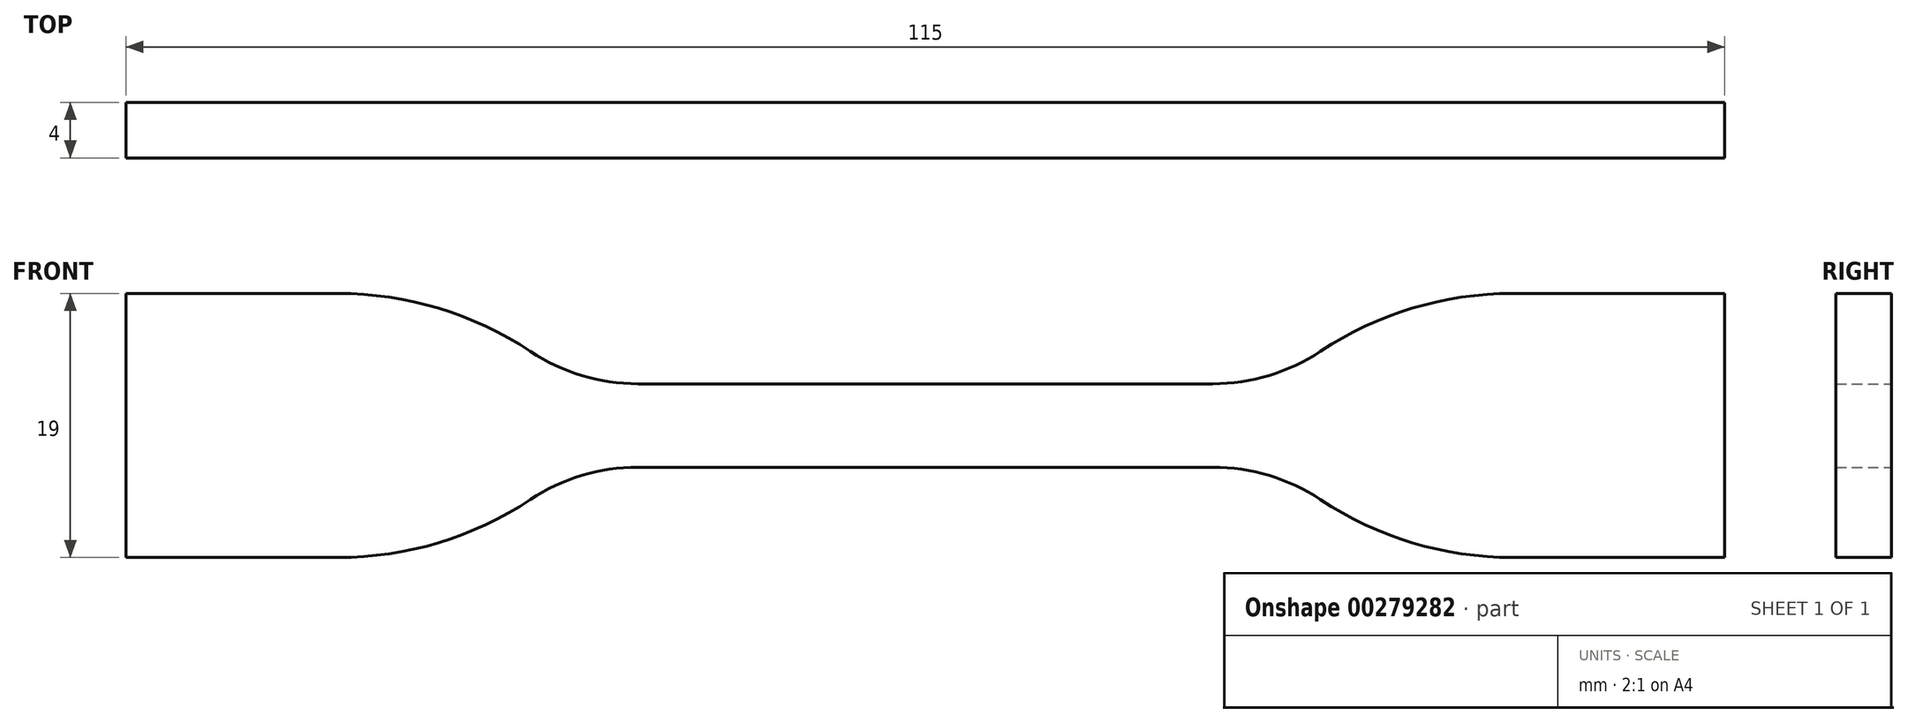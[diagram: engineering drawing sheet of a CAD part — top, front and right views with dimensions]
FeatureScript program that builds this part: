
annotation { "Feature Type Name" : "Feature", "Feature Type Description" : "" }
export const myFeature = defineFeature(function(context is Context, id is Id, definition is map)
    precondition{}
    {
        {
            var Q0;
            Q0=qCreatedBy(makeId("Front.planeOp"),FACE);
            var sketch = newSketch(context, id + "F0", { "sketchPlane" : qUnion([Q0])});
            skLineSegment(sketch, "E0", {"start": v(0, 3) * mm, "end": v(20.68, 3) * mm});
            skArc(sketch, "E1", {"start": v(20.68, 3) * mm, "mid": v(24.72, 3.6) * mm, "end": v(28.42, 5.33) * mm});
            skLineSegment(sketch, "E2", {"start": v(42.24, 9.5) * mm, "end": v(57.5, 9.5) * mm});
            skLineSegment(sketch, "E3.MirrorCS", {"start": v(42.24, -9.5) * mm, "end": v(57.5, -9.5) * mm});
            skLineSegment(sketch, "E4.MirrorCS", {"start": v(0, -3) * mm, "end": v(20.68, -3) * mm});
            skArc(sketch, "E5.MirrorCS", {"start": v(20.68, -3) * mm, "mid": v(24.72, -3.6) * mm, "end": v(28.42, -5.33) * mm});
            skArc(sketch, "E6.MirrorCS", {"start": v(-20.68, -3) * mm, "mid": v(-24.72, -3.6) * mm, "end": v(-28.42, -5.33) * mm});
            skLineSegment(sketch, "E7.MirrorCS", {"start": v(0, 3) * mm, "end": v(-20.68, 3) * mm});
            skArc(sketch, "E8.MirrorCS", {"start": v(-20.68, 3) * mm, "mid": v(-24.72, 3.6) * mm, "end": v(-28.42, 5.33) * mm});
            skLineSegment(sketch, "E9.MirrorCS", {"start": v(-42.24, -9.5) * mm, "end": v(-57.5, -9.5) * mm});
            skLineSegment(sketch, "E10.MirrorCS", {"start": v(0, -3) * mm, "end": v(-20.68, -3) * mm});
            skLineSegment(sketch, "E11.MirrorCS", {"start": v(-42.24, 9.5) * mm, "end": v(-57.5, 9.5) * mm});
            skLineSegment(sketch, "E12", {"start": v(-57.5, 9.5) * mm, "end": v(-57.5, -9.5) * mm});
            skLineSegment(sketch, "E13", {"start": v(57.5, 9.5) * mm, "end": v(57.5, -9.5) * mm});
            skPoint(sketch, "E14.visualSharp", {"position": v(32.5, 9.5) * mm});
            skArc(sketch, "E14.filletArc", {"start": v(42.24, 9.5) * mm, "mid": v(35.02, 8.44) * mm, "end": v(28.42, 5.33) * mm});
            skPoint(sketch, "E15.visualSharp", {"position": v(-32.5, 9.5) * mm});
            skArc(sketch, "E15.filletArc", {"start": v(-28.42, 5.33) * mm, "mid": v(-35.02, 8.44) * mm, "end": v(-42.24, 9.5) * mm});
            skPoint(sketch, "E16.visualSharp", {"position": v(-32.5, -9.5) * mm});
            skArc(sketch, "E16.filletArc", {"start": v(-42.24, -9.5) * mm, "mid": v(-35.02, -8.44) * mm, "end": v(-28.42, -5.33) * mm});
            skPoint(sketch, "E17.visualSharp", {"position": v(32.5, -9.5) * mm});
            skArc(sketch, "E17.filletArc", {"start": v(28.42, -5.33) * mm, "mid": v(35.02, -8.44) * mm, "end": v(42.24, -9.5) * mm});
            skSolve(sketch);
        }
        {
            var Q0;
            Q0 = qSketchRegion(id + "F0", true);
            extrude(context, id + "F1", {"entities" : qUnion([Q0]), "endBound" : BoundingType.SYMMETRIC, "depth" : 4 * mm});
        }
    });
